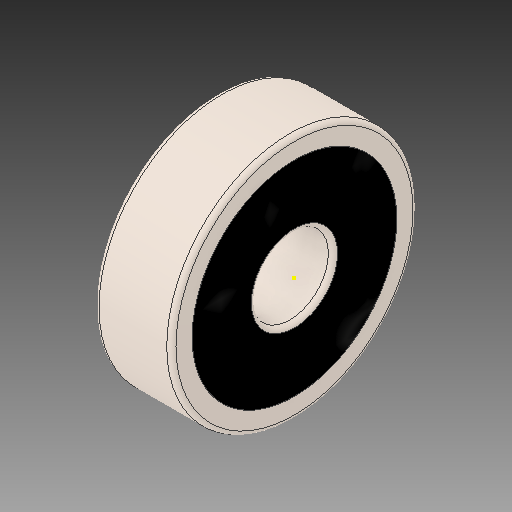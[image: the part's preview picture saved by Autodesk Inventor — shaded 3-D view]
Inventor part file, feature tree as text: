
AUTODESK INVENTOR PART (.ipt)
format: ipt  version: 2018 (Build 220112000, 112)  size: 2,295,808 bytes
history: imported  units: mm
features: other x22, sketch x3, imported_body x1
ambient origin geometry x8: Origin, YZ Plane, XZ Plane, XY Plane, X Axis, Y Axis, Z Axis, Center Point
bodies: Solid1 (imported_parasolid), Solid2 (imported_parasolid), Solid3 (imported_parasolid), Solid4 (imported_parasolid), Solid5 (imported_parasolid), Solid6 (imported_parasolid), Solid7 (imported_parasolid), Solid8 (imported_parasolid), Solid9 (imported_parasolid), Solid10 (imported_parasolid), Solid11 (imported_parasolid), Solid12 (imported_parasolid), Solid13 (imported_parasolid), Solid14 (imported_parasolid), Solid15 (imported_parasolid), Solid16 (imported_parasolid), Solid17 (imported_parasolid), Solid18 (imported_parasolid), Solid19 (imported_parasolid), Solid20 (imported_parasolid)
feature tree (26):
  other  "SKF 625.ipt"
  other  "Solid1::SKF 625.ipt"
  other  "Solid2::SKF 625.ipt"
  other  "Solid3::SKF 625.ipt"
  other  "Solid4::SKF 625.ipt"
  other  "Solid5::SKF 625.ipt"
  other  "Solid6::SKF 625.ipt"
  other  "Solid7::SKF 625.ipt"
  other  "Solid8::SKF 625.ipt"
  other  "Solid9::SKF 625.ipt"
  other  "Solid10::SKF 625.ipt"
  other  "Solid11::SKF 625.ipt"
  other  "Solid12::SKF 625.ipt"
  other  "Solid13::SKF 625.ipt"
  other  "Solid14::SKF 625.ipt"
  other  "Solid15::SKF 625.ipt"
  other  "Solid16::SKF 625.ipt"
  other  "Solid17::SKF 625.ipt"
  other  "Solid18::SKF 625.ipt"
  other  "Solid19::SKF 625.ipt"
  other  "Solid20::SKF 625.ipt"
  other  "TaggingFeature1"
  sketch  "Sketch1"  dims[d0=10.0mm]
  sketch  "Sketch2"
  sketch  "Sketch3"
  imported_body  NMx_Import_Brep_tag  [imported B-rep: ~49 faces, bbox_mm=None]
